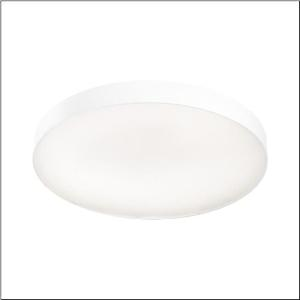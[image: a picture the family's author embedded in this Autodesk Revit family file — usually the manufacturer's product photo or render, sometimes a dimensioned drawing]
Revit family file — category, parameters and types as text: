
# Revit family: round_21_l_51mr38nd0421w
name_source: partatom
category: Lighting Fixtures
units: mm (PartAtom-declared; Revit-internal decimal feet)

## family parameters
Cut with Voids When Loaded = No
Host = Face
Light Source = No
Part Type = Normal
Room Calculation Point = No
Round Connector Dimension = Use Diameter
Shared = No

## types (1)
- Round 21 L (1 x LED, 12230 lm, 88.2 W, 4000K)
    Apparent Load = 88 VA
    CIE Flux Codes = 66 90 98 71 100
    Color Rendering = 80
    Color Temperature = 4000K
    Default Elevation = 1800 mm
    Description = Round 21 L, wall and ceiling luminaire, primary optical cover: micro prismatic cover, of PMMA, transparent, CAT 2 (L<= 3000cd/m²), light emission: direct/indirect distribution, primary light characteristic: symmetric, installation type: suspended mounting, surface-mounted, LED, rated luminous flux: 12.230lm, luminous efficacy: 139lm/W, light colour: 840, colour temperature: 4000K, with terminal, 5-pole, mains connection: 230V, AC, 50/60Hz, rated input power: 88W, housing, of aluminium, coated, white, diameter: 850mm, height: 62mm, protection rating (complete): IP40, insulation class (complete): insulation class I (protective earthing), certification: CE, impact resistance: IK04, permissible operating ambient temperature: -10..+35°C, packaging unit: 1 piece
    Height = 87 mm
    Lamp = 1 x LED
    Lamp Light Flux = 12230 lm
    Lamp Power = 88.2 W
    Lamp count = 1
    Length = 850 mm
    Luminous efficacy = 139 lm/W
    Manufacturer = Siteco
    ModVariant = No
    Model = 51MR38ND0421W
    Mounting Place = Ceiling
    Mounting Type = Surface mounted
    Number of Poles = 1
    OnlyDefault = Yes
    Power Factor = 1
    Product Name = Round 21 L
    Product group = wall and ceiling luminaire
    ProductGroupID = 303
    Protection Class = Protection class I
    Protection Degree = IP 40
    RLX_Detail_Level = 1
    RLX_Emergency_Light_Flux = 0 lm
    RLX_Emergency_Type = 0
    RLX_Emergency_Type_DB = No
    RlxData = <blob elided: 19477 chars, md5=9cf483d9>
    Socket = socket
    Standby Power = 0 W
    System Light Flux = 12230 lm
    System Power = 88 W
    Type Comments = Product without accessories
    Type Image = l_1258318.jpg
    URL = http://relux.com
    VarID = ---
    Voltage = 0 V
    Weight = 0.00 kg
    Width = 0 mm  [stored 0 ft]

note: [stored X ft] marks values corroborated as IEEE doubles in the binary element streams (Revit-internal decimal feet)

## geometry (parser evidence)
native form markers: Blend x4, Sweep x15
no freeform markers — native parametric forms only
